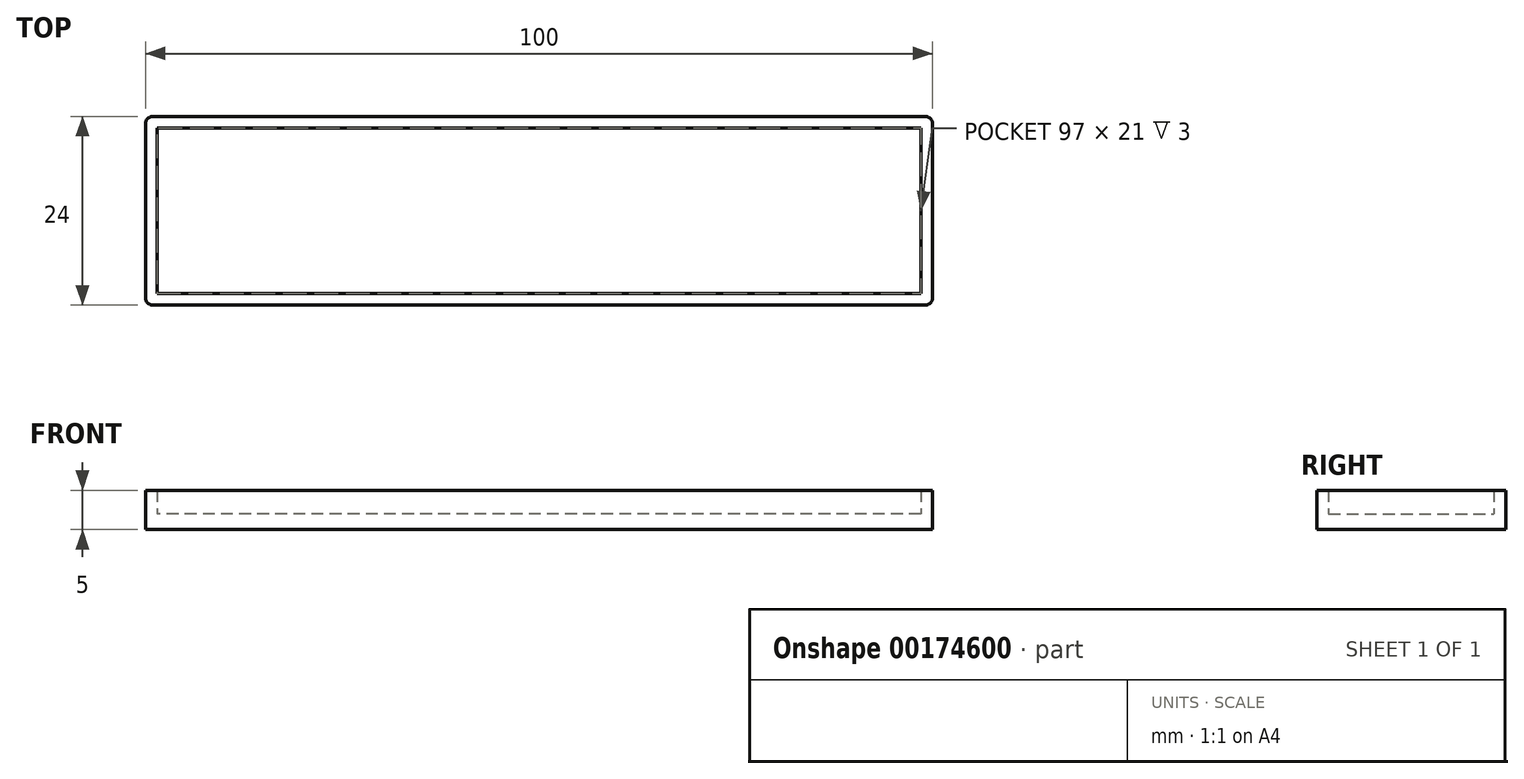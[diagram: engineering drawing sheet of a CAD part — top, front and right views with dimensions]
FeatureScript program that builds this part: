
annotation { "Feature Type Name" : "Feature", "Feature Type Description" : "" }
export const myFeature = defineFeature(function(context is Context, id is Id, definition is map)
    precondition{}
    {
        {
            var Q0;
            Q0=qCreatedBy(makeId("Top.planeOp"),FACE);
            var sketch = newSketch(context, id + "F0", { "sketchPlane" : qUnion([Q0])});
            skLineSegment(sketch, "E0.bottom", {"start": v(-24.36, 18.38) * mm, "end": v(72.64, 18.38) * mm});
            skLineSegment(sketch, "E0.top", {"start": v(-24.36, -2.62) * mm, "end": v(72.64, -2.62) * mm});
            skLineSegment(sketch, "E0.left", {"start": v(-24.36, 18.38) * mm, "end": v(-24.36, -2.62) * mm});
            skLineSegment(sketch, "E0.right", {"start": v(72.64, 18.38) * mm, "end": v(72.64, -2.62) * mm});
            skLineSegment(sketch, "E1.0", {"start": v(-25.86, 19.88) * mm, "end": v(74.14, 19.88) * mm});
            skLineSegment(sketch, "E1.1", {"start": v(-25.86, 19.88) * mm, "end": v(-25.86, -4.12) * mm});
            skLineSegment(sketch, "E1.2", {"start": v(-25.86, -4.12) * mm, "end": v(74.14, -4.12) * mm});
            skLineSegment(sketch, "E1.3", {"start": v(74.14, 19.88) * mm, "end": v(74.14, -4.12) * mm});
            skSolve(sketch);
        }
        {
            var Q0;
            Q0=makeQuery(id+"F0.imprint","IMPRINT",FACE,{"disambiguationData":[TD([[makeQuery(id+"F0.imprint","IMPRINT",EDGE,{"derivedFrom":sQuery(id+"F0.wireOp",EDGE,"E0.bottom")}),-1.0]])]});
            var Q1;
            Q1=makeQuery(id+"F0.imprint","IMPRINT",FACE,{"disambiguationData":[TD([[makeQuery(id+"F0.imprint","IMPRINT",EDGE,{"derivedFrom":sQuery(id+"F0.wireOp",EDGE,"E0.bottom")}),1.0]])]});
            extrude(context, id + "F1", {"entities" : qUnion([Q0, Q1]), "depth" : 2 * mm});
        }
        {
            var Q0;
            Q0=makeQuery(id+"F0.imprint","IMPRINT",FACE,{"disambiguationData":[TD([[makeQuery(id+"F0.imprint","IMPRINT",EDGE,{"derivedFrom":sQuery(id+"F0.wireOp",EDGE,"E0.bottom")}),1.0]])]});
            extrude(context, id + "F2", {"entities" : qUnion([Q0]), "operationType" : NewBodyOperationType.ADD, "depth" : 5 * mm});
        }
        {
            var Q0;
            {var subQ0=sQuery(id+"F0.wireOp",EDGE,"E1.3");var subQ1=sQuery(id+"F0.wireOp",EDGE,"E1.0");Q0=makeQuery(id+"F2.boolean.opBoolean","MERGE",EDGE,{"derivedFrom":[makeQuery(id+"F1.opExtrude","SWEPT_EDGE",EDGE,{"disambiguationData":[OSD([subQ1,subQ0])]}),makeQuery(id+"F2.opExtrude","SWEPT_EDGE",EDGE,{"disambiguationData":[OSD([subQ1,subQ0])]})]});}
            var Q1;
            {var subQ0=sQuery(id+"F0.wireOp",EDGE,"E1.3");var subQ1=sQuery(id+"F0.wireOp",EDGE,"E1.2");Q1=makeQuery(id+"F2.boolean.opBoolean","MERGE",EDGE,{"derivedFrom":[makeQuery(id+"F1.opExtrude","SWEPT_EDGE",EDGE,{"disambiguationData":[OSD([subQ1,subQ0])]}),makeQuery(id+"F2.opExtrude","SWEPT_EDGE",EDGE,{"disambiguationData":[OSD([subQ1,subQ0])]})]});}
            var Q2;
            {var subQ0=sQuery(id+"F0.wireOp",EDGE,"E1.2");var subQ1=sQuery(id+"F0.wireOp",EDGE,"E1.1");Q2=makeQuery(id+"F2.boolean.opBoolean","MERGE",EDGE,{"derivedFrom":[makeQuery(id+"F1.opExtrude","SWEPT_EDGE",EDGE,{"disambiguationData":[OSD([subQ1,subQ0])]}),makeQuery(id+"F2.opExtrude","SWEPT_EDGE",EDGE,{"disambiguationData":[OSD([subQ1,subQ0])]})]});}
            var Q3;
            {var subQ0=sQuery(id+"F0.wireOp",EDGE,"E1.1");var subQ1=sQuery(id+"F0.wireOp",EDGE,"E1.0");Q3=makeQuery(id+"F2.boolean.opBoolean","MERGE",EDGE,{"derivedFrom":[makeQuery(id+"F1.opExtrude","SWEPT_EDGE",EDGE,{"disambiguationData":[OSD([subQ1,subQ0])]}),makeQuery(id+"F2.opExtrude","SWEPT_EDGE",EDGE,{"disambiguationData":[OSD([subQ1,subQ0])]})]});}
            fillet(context, id + "F3", {"entities" : qUnion([Q0, Q1, Q2, Q3]), "radius" : 1 * mm, "tangentPropagation" : true, "allowEdgeOverflow" : false});
        }
    });
